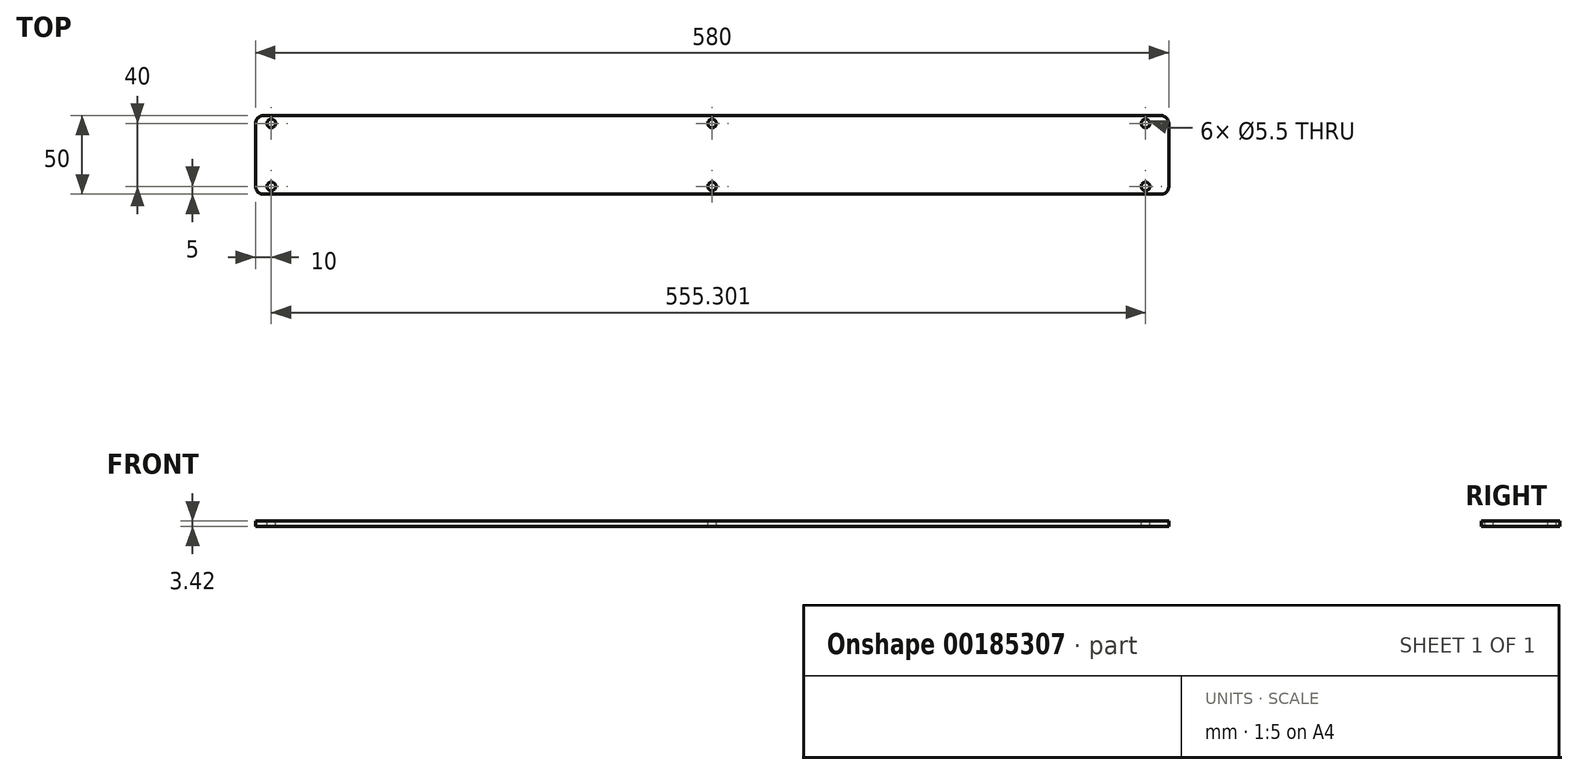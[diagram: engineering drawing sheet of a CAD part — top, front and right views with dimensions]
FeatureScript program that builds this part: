
annotation { "Feature Type Name" : "Feature", "Feature Type Description" : "" }
export const myFeature = defineFeature(function(context is Context, id is Id, definition is map)
    precondition{}
    {
        {
            var Q0;
            Q0=qCreatedBy(makeId("Top.planeOp"),FACE);
            var sketch = newSketch(context, id + "F0", { "sketchPlane" : qUnion([Q0])});
            skLineSegment(sketch, "E0.bottom", {"start": v(290, 25) * mm, "end": v(-290, 25) * mm});
            skLineSegment(sketch, "E0.top", {"start": v(290, -25) * mm, "end": v(-290, -25) * mm});
            skLineSegment(sketch, "E0.left", {"start": v(290, 25) * mm, "end": v(290, -25) * mm});
            skLineSegment(sketch, "E0.right", {"start": v(-290, 25) * mm, "end": v(-290, -25) * mm});
            skPoint(sketch, "E0.middle", {"position": v(0, 0) * mm});
            skSolve(sketch);
        }
        {
            var Q0;
            Q0 = qSketchRegion(id + "F0", true);
            extrude(context, id + "F1", {"entities" : qUnion([Q0]), "depth" : 3.42 * mm});
        }
        {
            var Q0;
            Q0=makeQuery(id+"F1.opExtrude","SWEPT_EDGE",EDGE,{"disambiguationData":[OSD([sQuery(id+"F0.wireOp",EDGE,"E0.bottom"),sQuery(id+"F0.wireOp",EDGE,"E0.right")])]});
            var Q1;
            Q1=makeQuery(id+"F1.opExtrude","SWEPT_EDGE",EDGE,{"disambiguationData":[OSD([sQuery(id+"F0.wireOp",EDGE,"E0.top"),sQuery(id+"F0.wireOp",EDGE,"E0.right")])]});
            var Q2;
            Q2=makeQuery(id+"F1.opExtrude","SWEPT_EDGE",EDGE,{"disambiguationData":[OSD([sQuery(id+"F0.wireOp",EDGE,"E0.bottom"),sQuery(id+"F0.wireOp",EDGE,"E0.left")])]});
            var Q3;
            Q3=makeQuery(id+"F1.opExtrude","SWEPT_EDGE",EDGE,{"disambiguationData":[OSD([sQuery(id+"F0.wireOp",EDGE,"E0.top"),sQuery(id+"F0.wireOp",EDGE,"E0.left")])]});
            fillet(context, id + "F2", {"entities" : qUnion([Q0, Q1, Q2, Q3]), "radius" : 5 * mm, "tangentPropagation" : true, "allowEdgeOverflow" : false});
        }
        {
            var Q0;
            Q0=makeQuery(id+"F1.opExtrude","CAP_FACE",FACE,{"disambiguationData":[OSD([sQuery(id+"F0.wireOp",EDGE,"E0.bottom"),sQuery(id+"F0.wireOp",EDGE,"E0.top"),sQuery(id+"F0.wireOp",EDGE,"E0.left"),sQuery(id+"F0.wireOp",EDGE,"E0.right")])],"isStart":false});
            var sketch = newSketch(context, id + "F3", { "sketchPlane" : qUnion([Q0])});
            skLineSegment(sketch, "E1", {"start": v(-280, 20) * mm, "end": v(-280, -20) * mm, "construction": true});
            skLineSegment(sketch, "E2", {"start": v(275.3, 20) * mm, "end": v(275.3, -20) * mm, "construction": true});
            skPoint(sketch, "E3.endSnap0", {"position": v(0, 25) * mm});
            skLineSegment(sketch, "E4", {"start": v(0, 20) * mm, "end": v(0, -20) * mm, "construction": true});
            skSolve(sketch);
        }
        {
            var Q0;
            Q0=sQuery(id+"F3.wireOp",VERTEX,"E1.end");
            var Q1;
            Q1=sQuery(id+"F3.wireOp",VERTEX,"E4.end");
            var Q2;
            Q2=sQuery(id+"F3.wireOp",VERTEX,"E2.end");
            var Q3;
            Q3=sQuery(id+"F3.wireOp",VERTEX,"E2.start");
            var Q4;
            Q4=sQuery(id+"F3.wireOp",VERTEX,"E4.start");
            var Q5;
            Q5=sQuery(id+"F3.wireOp",VERTEX,"E1.start");
            var Q6;
            Q6=makeQuery(id+"F1.opExtrude","SWEPT_BODY",BODY,{"disambiguationData":[OSD([sQuery(id+"F0.wireOp",EDGE,"E0.bottom"),sQuery(id+"F0.wireOp",EDGE,"E0.top"),sQuery(id+"F0.wireOp",EDGE,"E0.left"),sQuery(id+"F0.wireOp",EDGE,"E0.right")])]});
            hole(context, id + "F4", {"style" : HoleStyle.SIMPLE, "endStyle" : HoleEndStyle.THROUGH, "standardTappedOrClearance" : lookupTablePath({ "standard" : "ISO", "fit" : "Normal", "size" : "M5", "type" : "Clearance" }), "standardBlindInLast" : lookupTablePath({ "fit" : "Standard", "standard" : "ISO", "size" : "M5", "type" : "Clearance" }), "holeDiameter" : 5.5 * mm, "locations" : qUnion([Q0, Q1, Q2, Q3, Q4, Q5]), "scope" : qUnion([Q6]), "isTappedThrough" : true});
        }
    });
